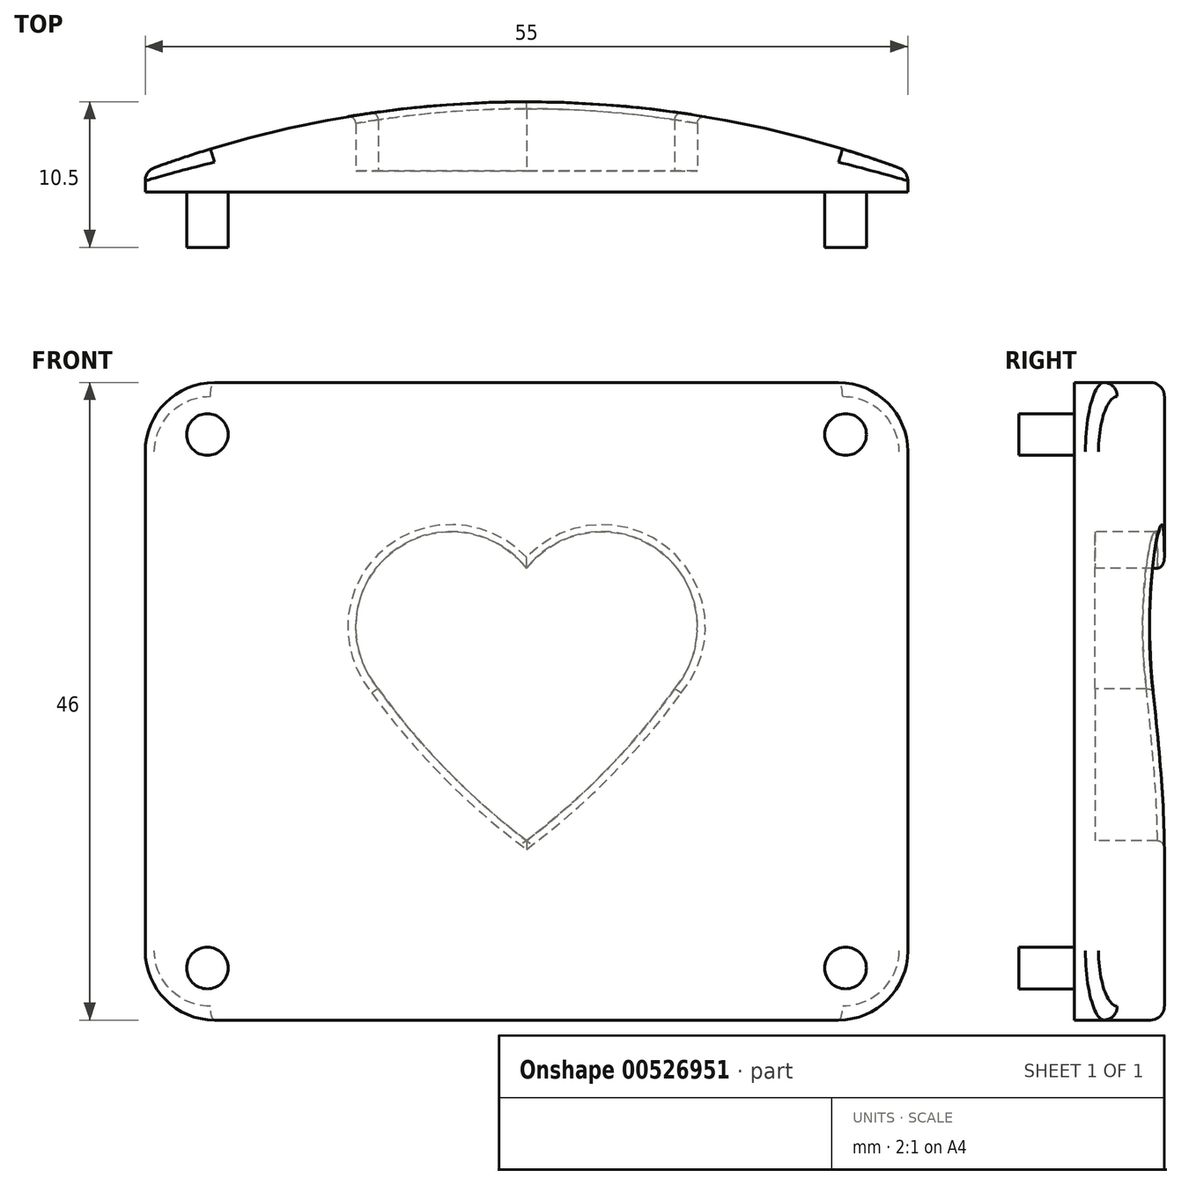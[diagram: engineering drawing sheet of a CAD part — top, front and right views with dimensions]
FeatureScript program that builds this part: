
annotation { "Feature Type Name" : "Feature", "Feature Type Description" : "" }
export const myFeature = defineFeature(function(context is Context, id is Id, definition is map)
    precondition{}
    {
        {
            var Q0;
            Q0=qCreatedBy(makeId("Top.planeOp"),FACE);
            var sketch = newSketch(context, id + "F0", { "sketchPlane" : qUnion([Q0])});
            skArc(sketch, "E0", {"start": v(27.5, 0) * mm, "mid": v(0, 5) * mm, "end": v(-27.5, 0) * mm});
            skLineSegment(sketch, "E1", {"start": v(-27.5, 0) * mm, "end": v(-27.5, -1.5) * mm});
            skLineSegment(sketch, "E2", {"start": v(-27.5, -1.5) * mm, "end": v(27.5, -1.5) * mm});
            skLineSegment(sketch, "E3", {"start": v(27.5, -1.5) * mm, "end": v(27.5, 0) * mm});
            skSolve(sketch);
        }
        {
            var Q0;
            Q0 = qSketchRegion(id + "F0", true);
            extrude(context, id + "F1", {"entities" : qUnion([Q0]), "depth" : 46 * mm, "offsetDistance" : 25 * mm, "symmetric" : true});
        }
        {
            var Q0;
            Q0=qCreatedBy(makeId("Front.planeOp"),FACE);
            var sketch = newSketch(context, id + "F2", { "sketchPlane" : qUnion([Q0])});
            skPoint(sketch, "E4.middle", {"position": v(0, 0) * mm});
            skPoint(sketch, "E5", {"position": v(-23.01, 19.25) * mm});
            skPoint(sketch, "E6", {"position": v(23.01, 19.25) * mm});
            skPoint(sketch, "E7", {"position": v(23.01, -19.25) * mm});
            skPoint(sketch, "E8", {"position": v(-23.01, -19.25) * mm});
            skCircle(sketch, "E9", {"center": v(-23.01, 19.25) * mm, "radius": 1.5 * mm});
            skCircle(sketch, "E10", {"center": v(23.01, 19.25) * mm, "radius": 1.5 * mm});
            skCircle(sketch, "E11", {"center": v(23.01, -19.25) * mm, "radius": 1.5 * mm});
            skCircle(sketch, "E12", {"center": v(-23.01, -19.25) * mm, "radius": 1.5 * mm});
            skPoint(sketch, "E13", {"position": v(0, -10.96) * mm});
            skSolve(sketch);
        }
        {
            var Q0;
            Q0=qCreatedBy(makeId("Front.planeOp"),FACE);
            var sketch = newSketch(context, id + "F3", { "sketchPlane" : qUnion([Q0])});
            skPoint(sketch, "E14.middle", {"position": v(0, 0.9) * mm});
            skPoint(sketch, "E15", {"position": v(-23.01, 20.15) * mm});
            skPoint(sketch, "E16", {"position": v(23.01, 20.15) * mm});
            skPoint(sketch, "E17", {"position": v(23.01, -18.34) * mm});
            skPoint(sketch, "E18", {"position": v(-23.01, -18.34) * mm});
            skCircle(sketch, "E19", {"center": v(5.43, 5.35) * mm, "radius": 6.9 * mm});
            skPoint(sketch, "E20", {"position": v(0, -10.05) * mm});
            skArc(sketch, "E21", {"start": v(0, -10.05) * mm, "mid": v(5.75, -4.97) * mm, "end": v(10.69, 0.9) * mm});
            skCircle(sketch, "E22.MirrorC", {"center": v(-5.43, 5.35) * mm, "radius": 6.9 * mm});
            skArc(sketch, "E23.MirrorCS", {"start": v(0, -10.05) * mm, "mid": v(-5.75, -4.97) * mm, "end": v(-10.69, 0.9) * mm});
            skSolve(sketch);
        }
        {
            var Q0;
            Q0 = qSketchRegion(id + "F2", true);
            extrude(context, id + "F4", {"entities" : qUnion([Q0]), "operationType" : NewBodyOperationType.ADD, "depth" : 5.5 * mm, "offsetDistance" : 25 * mm});
        }
        {
            var Q0;
            Q0 = qSketchRegion(id + "F3", true);
            extrude(context, id + "F5", {"entities" : qUnion([Q0]), "operationType" : NewBodyOperationType.REMOVE, "oppositeDirection" : true, "depth" : 10 * mm, "offsetDistance" : 25 * mm});
        }
        {
            var Q0;
            Q0=makeQuery(id+"F1.opExtrude","CAP_EDGE",EDGE,{"disambiguationData":[OSD([sQuery(id+"F0.wireOp",EDGE,"E1")])],"isStart":false});
            var Q1;
            Q1=makeQuery(id+"F1.opExtrude","CAP_EDGE",EDGE,{"disambiguationData":[OSD([sQuery(id+"F0.wireOp",EDGE,"E3")])],"isStart":true});
            var Q2;
            Q2=makeQuery(id+"F1.opExtrude","CAP_EDGE",EDGE,{"disambiguationData":[OSD([sQuery(id+"F0.wireOp",EDGE,"E1")])],"isStart":true});
            var Q3;
            Q3=makeQuery(id+"F1.opExtrude","CAP_EDGE",EDGE,{"disambiguationData":[OSD([sQuery(id+"F0.wireOp",EDGE,"E3")])],"isStart":false});
            fillet(context, id + "F6", {"entities" : qUnion([Q0, Q1, Q2, Q3]), "radius" : 5 * mm, "tangentPropagation" : true, "allowEdgeOverflow" : false});
        }
        {
            var Q0;
            Q0=makeQuery(id+"F1.opExtrude","CAP_EDGE",EDGE,{"disambiguationData":[OSD([sQuery(id+"F0.wireOp",EDGE,"E0")])],"isStart":false});
            var Q1;
            Q1=makeQuery(id+"F1.opExtrude","CAP_EDGE",EDGE,{"disambiguationData":[OSD([sQuery(id+"F0.wireOp",EDGE,"E0")])],"isStart":true});
            var Q2;
            Q2=makeQuery(id+"F1.opExtrude","SWEPT_EDGE",EDGE,{"disambiguationData":[OSD([sQuery(id+"F0.wireOp",EDGE,"E0"),sQuery(id+"F0.wireOp",EDGE,"E1")])]});
            var Q3;
            Q3=makeQuery(id+"F1.opExtrude","SWEPT_EDGE",EDGE,{"disambiguationData":[OSD([sQuery(id+"F0.wireOp",EDGE,"E0"),sQuery(id+"F0.wireOp",EDGE,"E3")])]});
            fillet(context, id + "F7", {"entities" : qUnion([Q0, Q1, Q2, Q3]), "radius" : 1 * mm, "tangentPropagation" : true, "allowEdgeOverflow" : false});
        }
        {
            var Q0;
            Q0=makeQuery(id+"F5.boolean.opBoolean","INTERSECT",EDGE,{"derivedFrom":[makeQuery(id+"F1.opExtrude","SWEPT_FACE",FACE,{"disambiguationData":[OSD([sQuery(id+"F0.wireOp",EDGE,"E0")])]}),makeQuery(id+"F5.opExtrude","SWEPT_FACE",FACE,{"disambiguationData":[OSD([sQuery(id+"F3.wireOp",EDGE,"E22.MirrorC")])]})]});
            var Q1;
            Q1=makeQuery(id+"F5.boolean.opBoolean","INTERSECT",EDGE,{"derivedFrom":[makeQuery(id+"F1.opExtrude","SWEPT_FACE",FACE,{"disambiguationData":[OSD([sQuery(id+"F0.wireOp",EDGE,"E0")])]}),makeQuery(id+"F5.opExtrude","SWEPT_FACE",FACE,{"disambiguationData":[OSD([sQuery(id+"F3.wireOp",EDGE,"E19")])]})]});
            var Q2;
            Q2=makeQuery(id+"F5.boolean.opBoolean","INTERSECT",EDGE,{"derivedFrom":[makeQuery(id+"F1.opExtrude","SWEPT_FACE",FACE,{"disambiguationData":[OSD([sQuery(id+"F0.wireOp",EDGE,"E0")])]}),makeQuery(id+"F5.opExtrude","SWEPT_FACE",FACE,{"disambiguationData":[OSD([sQuery(id+"F3.wireOp",EDGE,"E21")])]})]});
            var Q3;
            Q3=makeQuery(id+"F5.boolean.opBoolean","INTERSECT",EDGE,{"derivedFrom":[makeQuery(id+"F1.opExtrude","SWEPT_FACE",FACE,{"disambiguationData":[OSD([sQuery(id+"F0.wireOp",EDGE,"E0")])]}),makeQuery(id+"F5.opExtrude","SWEPT_FACE",FACE,{"disambiguationData":[OSD([sQuery(id+"F3.wireOp",EDGE,"E23.MirrorCS")])]})]});
            fillet(context, id + "F8", {"entities" : qUnion([Q0, Q1, Q2, Q3]), "radius" : 0.5 * mm, "tangentPropagation" : true, "allowEdgeOverflow" : false});
        }
    });
